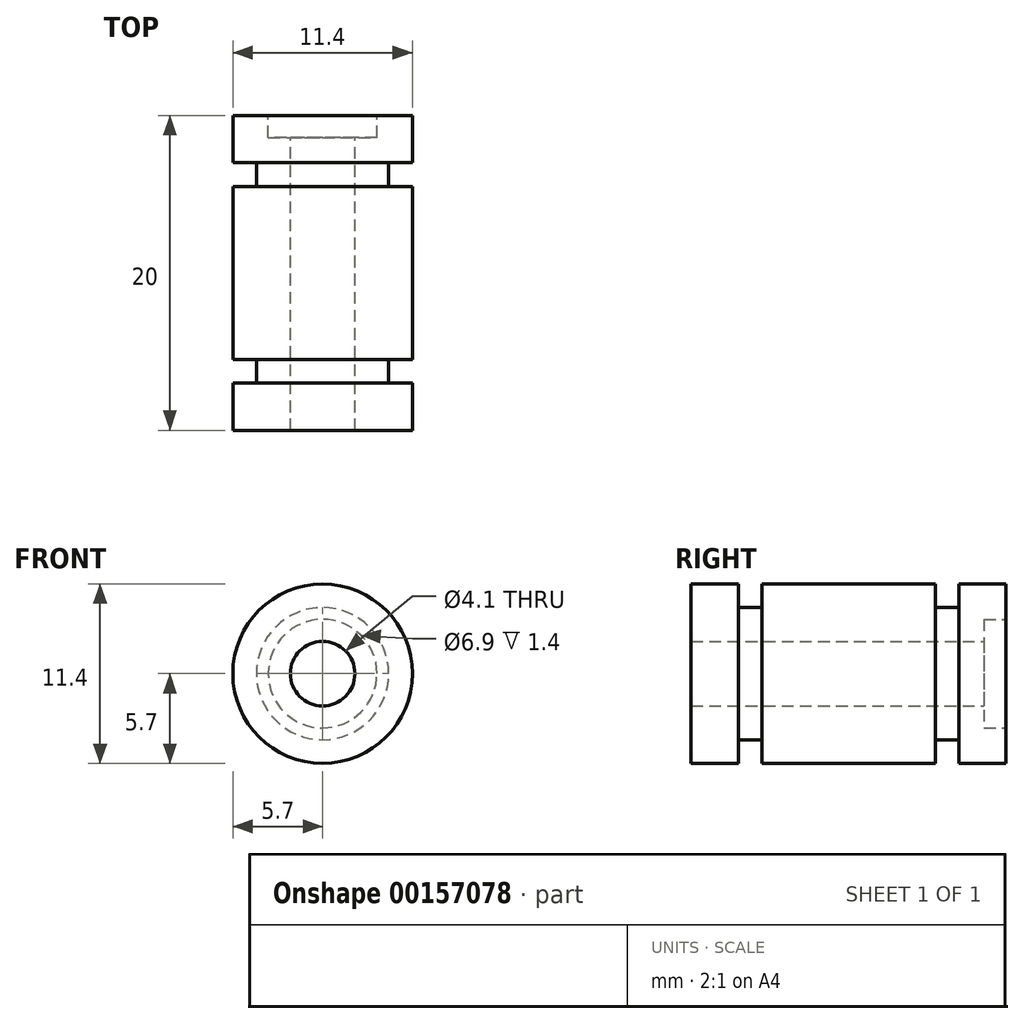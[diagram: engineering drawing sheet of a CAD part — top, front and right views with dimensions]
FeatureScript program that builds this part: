
annotation { "Feature Type Name" : "Feature", "Feature Type Description" : "" }
export const myFeature = defineFeature(function(context is Context, id is Id, definition is map)
    precondition{}
    {
        {
            var Q0;
            Q0=qCreatedBy(makeId("Right.planeOp"),FACE);
            var sketch = newSketch(context, id + "F0", { "sketchPlane" : qUnion([Q0])});
            skLineSegment(sketch, "E0", {"start": v(11.47, 0) * mm, "end": v(0, 0) * mm, "construction": true});
            skLineSegment(sketch, "E1", {"start": v(18.6, 2.05) * mm, "end": v(0, 2.05) * mm});
            skLineSegment(sketch, "E2", {"start": v(18.6, 2.05) * mm, "end": v(18.6, 3.45) * mm});
            skLineSegment(sketch, "E3", {"start": v(20, 3.45) * mm, "end": v(18.6, 3.45) * mm});
            skLineSegment(sketch, "E4", {"start": v(20, 3.45) * mm, "end": v(20, 5.7) * mm});
            skLineSegment(sketch, "E5", {"start": v(17, 5.7) * mm, "end": v(20, 5.7) * mm});
            skLineSegment(sketch, "E6", {"start": v(17, 5.7) * mm, "end": v(17, 4.2) * mm});
            skLineSegment(sketch, "E7", {"start": v(15.5, 4.2) * mm, "end": v(17, 4.2) * mm});
            skLineSegment(sketch, "E8", {"start": v(3, 4.2) * mm, "end": v(3, 5.7) * mm});
            skLineSegment(sketch, "E9", {"start": v(0, 5.7) * mm, "end": v(3, 5.7) * mm});
            skLineSegment(sketch, "E10", {"start": v(0, 5.7) * mm, "end": v(0, 2.05) * mm});
            skLineSegment(sketch, "E11", {"start": v(4.5, 4.2) * mm, "end": v(4.5, 5.7) * mm});
            skLineSegment(sketch, "E12", {"start": v(4.5, 5.7) * mm, "end": v(15.5, 5.7) * mm});
            skLineSegment(sketch, "E13", {"start": v(15.5, 5.7) * mm, "end": v(15.5, 4.2) * mm});
            skLineSegment(sketch, "E14.trimOffspring", {"start": v(4.5, 4.2) * mm, "end": v(3, 4.2) * mm});
            skSolve(sketch);
        }
        {
            var Q0;
            Q0=makeQuery(id+"F0.imprint","IMPRINT",FACE,{"disambiguationData":[TD([[makeQuery(id+"F0.imprint","IMPRINT",EDGE,{"derivedFrom":sQuery(id+"F0.wireOp",EDGE,"E1")}),-1.0]])]});
            var Q1;
            Q1=sQuery(id+"F0.wireOp",EDGE,"E0");
            revolve(context, id + "F1", {"entities" : qUnion([Q0]), "axis" : qUnion([Q1]), "revolveType" : RevolveType.FULL});
        }
    });
